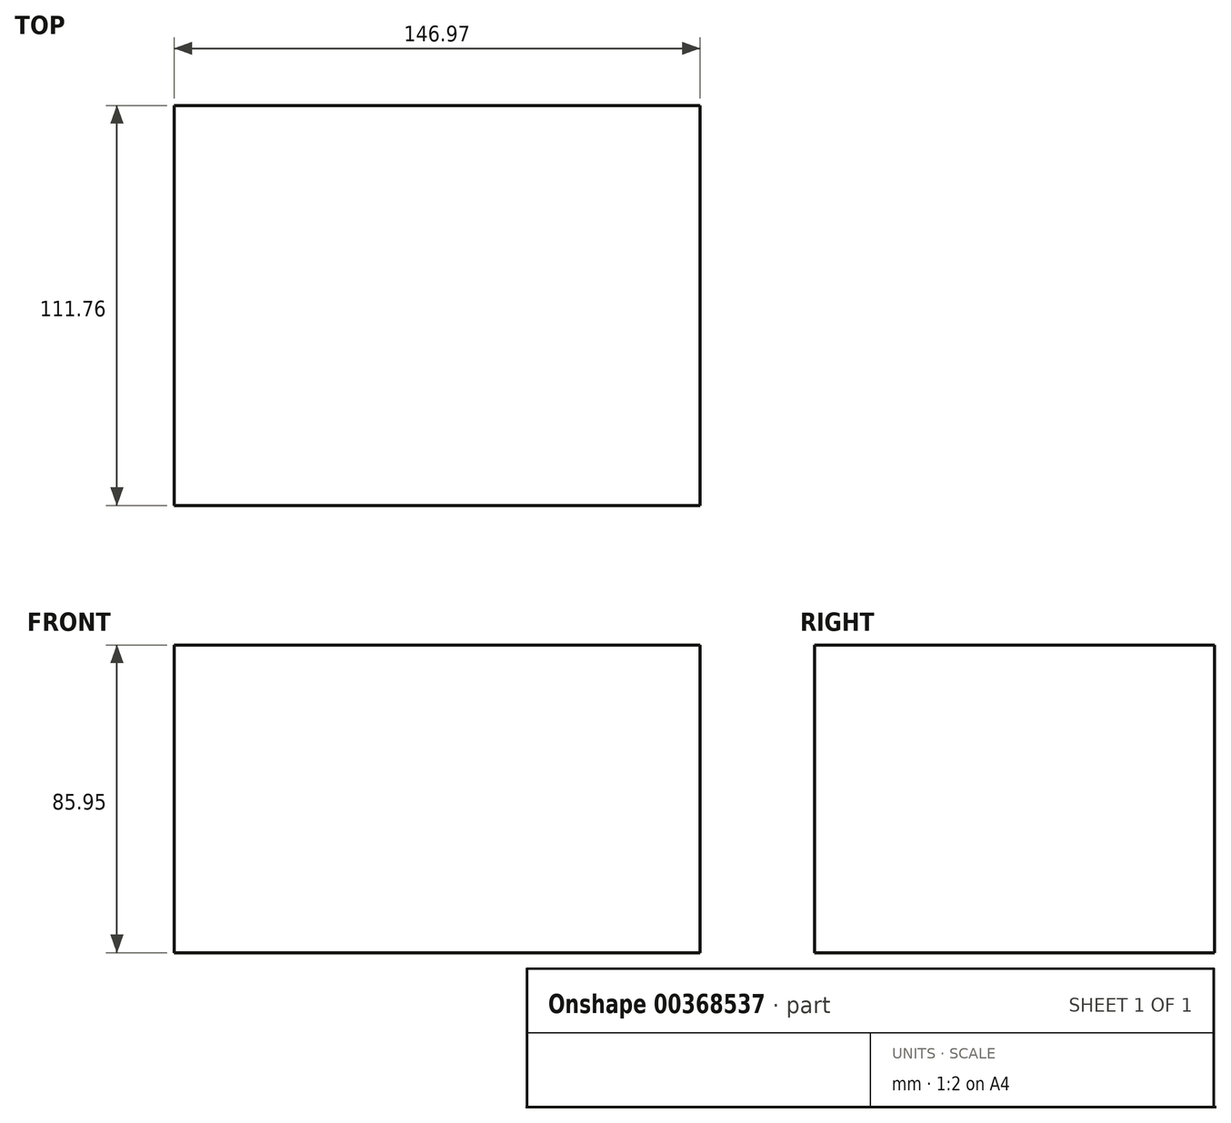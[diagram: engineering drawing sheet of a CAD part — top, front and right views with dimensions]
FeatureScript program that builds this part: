
annotation { "Feature Type Name" : "Feature", "Feature Type Description" : "" }
export const myFeature = defineFeature(function(context is Context, id is Id, definition is map)
    precondition{}
    {
        {
            var Q0;
            Q0=qCreatedBy(makeId("Front.planeOp"),FACE);
            var sketch = newSketch(context, id + "F0", { "sketchPlane" : qUnion([Q0])});
            skLineSegment(sketch, "E0.bottom", {"start": v(-58.58, 51.84) * mm, "end": v(88.4, 51.84) * mm});
            skLineSegment(sketch, "E0.top", {"start": v(-58.58, -34.11) * mm, "end": v(88.4, -34.11) * mm});
            skLineSegment(sketch, "E0.left", {"start": v(-58.58, 51.84) * mm, "end": v(-58.58, -34.11) * mm});
            skLineSegment(sketch, "E0.right", {"start": v(88.4, 51.84) * mm, "end": v(88.4, -34.11) * mm});
            skSolve(sketch);
        }
        {
            var Q0;
            Q0 = qSketchRegion(id + "F0", true);
            extrude(context, id + "F1", {"entities" : qUnion([Q0]), "depth" : 111.76 * mm});
        }
    });
